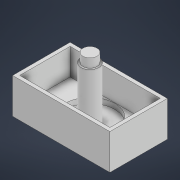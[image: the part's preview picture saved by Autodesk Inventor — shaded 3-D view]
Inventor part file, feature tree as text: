
AUTODESK INVENTOR PART (.ipt)
format: ipt  version: 2021 (Build 250183000, 183)  size: 128,000 bytes
history: native  units: mm
features: extrude x5, sketch x5
ambient origin geometry x8: Origin, YZ Plane, XZ Plane, XY Plane, X Axis, Y Axis, Z Axis, Center Point
bodies: Volumenkörper1 (feature_tree)
feature tree (10):
  extrude  "Extrusion1"  Depth=32.5mm
  extrude  "Extrusion2"  Depth=5.0mm
  extrude  "Extrusion3"  Depth=3.0mm TaperAngle=0.0deg
  extrude  "Extrusion4"  Depth=30.0mm TaperAngle=0.0deg
  extrude  "Extrusion5"  Depth=5.0mm TaperAngle=0.0deg
  sketch  "Skizze1"  dims[d0=55.0mm d1=32.5mm]
  sketch  "Skizze2"  dims[d2=5.0mm d3=0.0mm d4=28.0mm]
  sketch  "Skizze3"  dims[d5=3.0mm d6=3.0mm d7=0.0mm]
  sketch  "Skizze4"  dims[d8=10.0mm d9=30.0mm d10=0.0mm]
  sketch  "Skizze5"  dims[d11=8.0mm d12=5.0mm d13=0.0mm d14=2.0mm d15=15.0mm d16=0.0mm]
